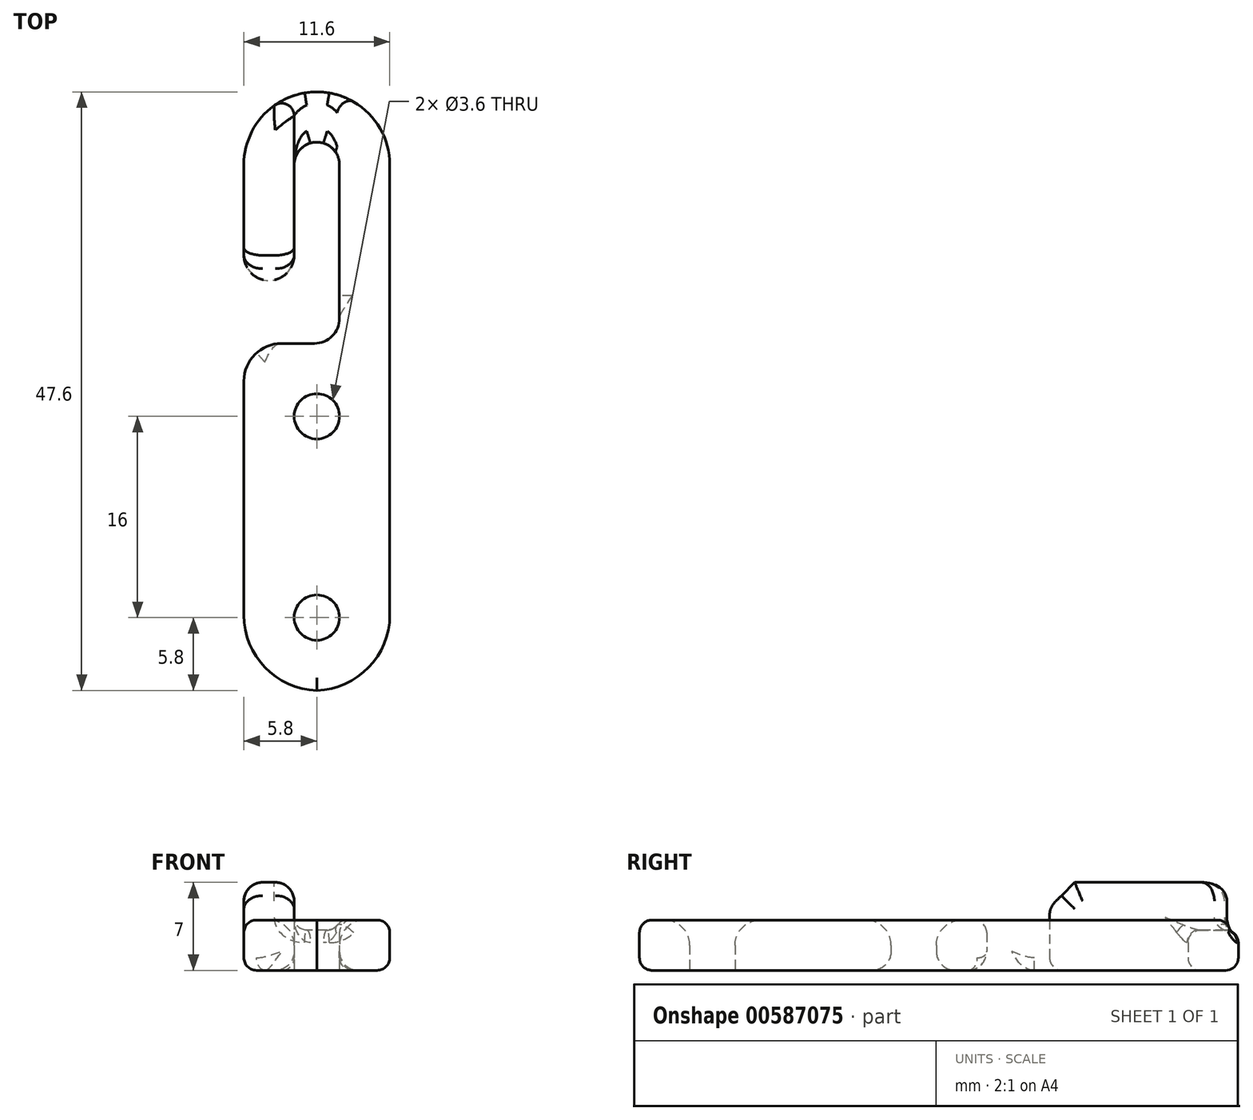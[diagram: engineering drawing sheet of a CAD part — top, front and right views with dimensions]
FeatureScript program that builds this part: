
annotation { "Feature Type Name" : "Feature", "Feature Type Description" : "" }
export const myFeature = defineFeature(function(context is Context, id is Id, definition is map)
    precondition{}
    {
        {
            var Q0;
            Q0=qCreatedBy(makeId("Top.planeOp"),FACE);
            var sketch = newSketch(context, id + "F0", { "sketchPlane" : qUnion([Q0])});
            skCircle(sketch, "E0", {"center": v(0, 0) * mm, "radius": 1.8 * mm});
            skCircle(sketch, "E1", {"center": v(0, -16) * mm, "radius": 1.8 * mm});
            skLineSegment(sketch, "E2", {"start": v(0, 0) * mm, "end": v(0, 20) * mm, "construction": true});
            skLineSegment(sketch, "E3", {"start": v(0, 0) * mm, "end": v(0, -16) * mm, "construction": true});
            skLineSegment(sketch, "E4.top", {"start": v(0.2, -21.8) * mm, "end": v(-0.2, -21.8) * mm});
            skLineSegment(sketch, "E4.left", {"start": v(5.8, 20) * mm, "end": v(5.8, 12.8) * mm});
            skLineSegment(sketch, "E4.right", {"start": v(-5.8, 2.8) * mm, "end": v(-5.8, -15.8) * mm});
            skPoint(sketch, "E5.visualSharp", {"position": v(5.8, -21.8) * mm});
            skArc(sketch, "E5.filletArc", {"start": v(-0.2, -21.8) * mm, "mid": v(4.04, -20.04) * mm, "end": v(5.8, -15.8) * mm});
            skPoint(sketch, "E6.visualSharp", {"position": v(-5.8, -21.8) * mm});
            skArc(sketch, "E6.filletArc", {"start": v(-5.8, -15.8) * mm, "mid": v(-4.04, -20.04) * mm, "end": v(0.2, -21.8) * mm});
            skLineSegment(sketch, "E7", {"start": v(0, 20) * mm, "end": v(1.8, 20) * mm, "construction": true});
            skLineSegment(sketch, "E8.trimOffspring", {"start": v(5.8, 12.8) * mm, "end": v(5.8, -15.8) * mm});
            skLineSegment(sketch, "E9", {"start": v(-1.8, 20) * mm, "end": v(-1.8, 12.8) * mm});
            skLineSegment(sketch, "E10", {"start": v(1.8, 20) * mm, "end": v(1.8, 7.8) * mm});
            skPoint(sketch, "E11.trimOffspring.start.orphan", {"position": v(-1.8, 12.8) * mm});
            skArc(sketch, "E12", {"start": v(1.8, 20) * mm, "mid": v(0, 21.8) * mm, "end": v(-1.8, 20) * mm});
            skArc(sketch, "E13", {"start": v(-5.8, 20) * mm, "mid": v(0, 25.8) * mm, "end": v(5.8, 20) * mm});
            skLineSegment(sketch, "E14", {"start": v(-5.8, 20) * mm, "end": v(-5.8, 12.8) * mm});
            skArc(sketch, "E15", {"start": v(-5.8, 12.8) * mm, "mid": v(-3.8, 10.8) * mm, "end": v(-1.8, 12.8) * mm});
            skPoint(sketch, "E16.orphan", {"position": v(-1.8, 5.8) * mm});
            skLineSegment(sketch, "E17", {"start": v(-2.8, 5.8) * mm, "end": v(-0.2, 5.8) * mm});
            skPoint(sketch, "E18.orphan", {"position": v(1.8, 12.8) * mm});
            skPoint(sketch, "E19.visualSharp", {"position": v(-5.8, 5.8) * mm});
            skArc(sketch, "E19.filletArc", {"start": v(-2.8, 5.8) * mm, "mid": v(-4.92, 4.92) * mm, "end": v(-5.8, 2.8) * mm});
            skPoint(sketch, "E20.visualSharp", {"position": v(1.8, 5.8) * mm});
            skArc(sketch, "E20.filletArc", {"start": v(-0.2, 5.8) * mm, "mid": v(1.21, 6.39) * mm, "end": v(1.8, 7.8) * mm});
            skSolve(sketch);
        }
        {
            var Q0;
            Q0=makeQuery(id+"F0.imprint","IMPRINT",FACE,{"disambiguationData":[TD([[makeQuery(id+"F0.imprint","IMPRINT",EDGE,{"derivedFrom":sQuery(id+"F0.wireOp",EDGE,"E0")}),-1.0]])]});
            extrude(context, id + "F1", {"entities" : qUnion([Q0]), "depth" : 4 * mm, "offsetDistance" : 25 * mm});
        }
        {
            var Q0;
            Q0=makeQuery(id+"F1.opExtrude","CAP_EDGE",EDGE,{"disambiguationData":[OSD([sQuery(id+"F0.wireOp",EDGE,"E0")])],"isStart":false});
            var Q1;
            Q1=makeQuery(id+"F1.opExtrude","CAP_EDGE",EDGE,{"disambiguationData":[OSD([sQuery(id+"F0.wireOp",EDGE,"E1")])],"isStart":false});
            fillet(context, id + "F2", {"entities" : qUnion([Q0, Q1]), "radius" : 2 * mm, "tangentPropagation" : true, "allowEdgeOverflow" : false});
        }
        {
            var Q0;
            Q0=makeQuery(id+"F1.opExtrude","CAP_EDGE",EDGE,{"disambiguationData":[OSD([sQuery(id+"F0.wireOp",EDGE,"E0")])],"isStart":true});
            var Q1;
            Q1=makeQuery(id+"F1.opExtrude","CAP_EDGE",EDGE,{"disambiguationData":[OSD([sQuery(id+"F0.wireOp",EDGE,"RurybiIE-2Qs8-uj2R-1JhG-sVs6zd4Z8fUQ")])],"isStart":true});
            var Q2;
            Q2=makeQuery(id+"F1.opExtrude","CAP_EDGE",EDGE,{"disambiguationData":[OSD([sQuery(id+"F0.wireOp",EDGE,"315a471d-3a10-48b4-a05f-508db2f02c06.filletArc")])],"isStart":true});
            fillet(context, id + "F3", {"entities" : qUnion([Q0, Q1, Q2]), "radius" : 1.5 * mm, "allowEdgeOverflow" : false});
        }
        {
            var Q0;
            Q0=makeQuery(id+"F1.opExtrude","CAP_EDGE",EDGE,{"disambiguationData":[OSD([sQuery(id+"F0.wireOp",EDGE,"E17")])],"isStart":true});
            var Q1;
            Q1=makeQuery(id+"F1.opExtrude","CAP_EDGE",EDGE,{"disambiguationData":[OSD([sQuery(id+"F0.wireOp",EDGE,"E20.filletArc")])],"isStart":true});
            fillet(context, id + "F4", {"entities" : qUnion([Q0, Q1]), "radius" : 1.5 * mm, "allowEdgeOverflow" : false});
        }
        {
            var Q0;
            Q0=makeQuery(id+"F1.opExtrude","CAP_FACE",FACE,{"disambiguationData":[OSD([sQuery(id+"F0.wireOp",EDGE,"E0"),sQuery(id+"F0.wireOp",EDGE,"E1"),sQuery(id+"F0.wireOp",EDGE,"E4.left"),sQuery(id+"F0.wireOp",EDGE,"E4.right"),sQuery(id+"F0.wireOp",EDGE,"E5.filletArc"),sQuery(id+"F0.wireOp",EDGE,"E6.filletArc"),sQuery(id+"F0.wireOp",EDGE,"E8.trimOffspring"),sQuery(id+"F0.wireOp",EDGE,"E9"),sQuery(id+"F0.wireOp",EDGE,"E10"),sQuery(id+"F0.wireOp",EDGE,"E12"),sQuery(id+"F0.wireOp",EDGE,"E13"),sQuery(id+"F0.wireOp",EDGE,"E14"),sQuery(id+"F0.wireOp",EDGE,"E15"),sQuery(id+"F0.wireOp",EDGE,"E17"),sQuery(id+"F0.wireOp",EDGE,"E19.filletArc"),sQuery(id+"F0.wireOp",EDGE,"E20.filletArc")])],"isStart":false});
            var sketch = newSketch(context, id + "F5", { "sketchPlane" : qUnion([Q0])});
            skArc(sketch, "E21.0.0", {"start": v(-5.8, -15.8) * mm, "mid": v(-4.11, -19.97) * mm, "end": v(0, -21.8) * mm});
            skArc(sketch, "E21.0.1", {"start": v(0, -21.8) * mm, "mid": v(4.11, -19.97) * mm, "end": v(5.8, -15.8) * mm});
            skLineSegment(sketch, "E21.0.2", {"start": v(5.8, -15.8) * mm, "end": v(5.8, 20) * mm});
            skArc(sketch, "E21.0.3", {"start": v(5.8, 20) * mm, "mid": v(0, 25.8) * mm, "end": v(-5.8, 20) * mm});
            skLineSegment(sketch, "E21.0.4", {"start": v(-5.8, 20) * mm, "end": v(-5.8, 12.8) * mm});
            skArc(sketch, "E21.0.5", {"start": v(-5.8, 12.8) * mm, "mid": v(-3.8, 10.8) * mm, "end": v(-1.8, 12.8) * mm});
            skLineSegment(sketch, "E21.0.6", {"start": v(-1.8, 12.8) * mm, "end": v(-1.8, 20) * mm});
            skArc(sketch, "E21.0.7", {"start": v(-1.8, 20) * mm, "mid": v(0, 21.8) * mm, "end": v(1.8, 20) * mm});
            skLineSegment(sketch, "E21.0.8", {"start": v(1.8, 20) * mm, "end": v(1.8, 7.8) * mm});
            skArc(sketch, "E21.0.9", {"start": v(1.8, 7.8) * mm, "mid": v(1.21, 6.39) * mm, "end": v(-0.2, 5.8) * mm});
            skLineSegment(sketch, "E21.0.10", {"start": v(-0.2, 5.8) * mm, "end": v(-2.8, 5.8) * mm});
            skArc(sketch, "E21.0.11", {"start": v(-2.8, 5.8) * mm, "mid": v(-4.92, 4.92) * mm, "end": v(-5.8, 2.8) * mm});
            skLineSegment(sketch, "E21.0.12", {"start": v(-5.8, 2.8) * mm, "end": v(-5.8, -15.8) * mm});
            skLineSegment(sketch, "E22", {"start": v(-1.8, 20) * mm, "end": v(-5.8, 20) * mm});
            skLineSegment(sketch, "E23", {"start": v(-1.8, 12.8) * mm, "end": v(-5.8, 12.8) * mm});
            skLineSegment(sketch, "E24", {"start": v(-1.8, 20) * mm, "end": v(-1.8, 30.41) * mm});
            skSolve(sketch);
        }
        {
            var Q0;
            Q0=makeQuery(id+"F5.imprint","IMPRINT",FACE,{"disambiguationData":[TD([[makeQuery(id+"F5.imprint","IMPRINT",EDGE,{"derivedFrom":sQuery(id+"F5.wireOp",EDGE,"E21.0.4")}),1.0]])]});
            var Q1;
            {var subQ0=sQuery(id+"F5.wireOp",EDGE,"E22");Q1=makeQuery(id+"F5.imprint","IMPRINT",FACE,{"disambiguationData":[TD([[makeQuery(id+"F5.imprint","IMPRINT",EDGE,{"derivedFrom":subQ0}),-1.0]])]});}
            var Q2;
            Q2=makeQuery(id+"F5.imprint","IMPRINT",FACE,{"disambiguationData":[TD([[makeQuery(id+"F5.imprint","IMPRINT",EDGE,{"derivedFrom":sQuery(id+"F5.wireOp",EDGE,"E21.0.5")}),1.0]])]});
            extrude(context, id + "F6", {"entities" : qUnion([Q0, Q1, Q2]), "operationType" : NewBodyOperationType.ADD, "depth" : 3 * mm, "offsetDistance" : 25 * mm});
        }
        {
            var Q0;
            Q0=makeQuery(id+"F6.boolean.opBoolean","MERGE",FACE,{"derivedFrom":[makeQuery(id+"F1.opExtrude","SWEPT_FACE",FACE,{"disambiguationData":[OSD([sQuery(id+"F0.wireOp",EDGE,"E14")])]}),makeQuery(id+"F6.opExtrude","SWEPT_FACE",FACE,{"disambiguationData":[OSD([sQuery(id+"F5.wireOp",EDGE,"E21.0.4")])]})]});
            var sketch = newSketch(context, id + "F7", { "sketchPlane" : qUnion([Q0])});
            skPoint(sketch, "E25.1", {"position": v(-12.8, 7) * mm});
            skLineSegment(sketch, "E25.2", {"start": v(-20, 7) * mm, "end": v(-12.8, 7) * mm});
            skLineSegment(sketch, "E25.3", {"start": v(-12.8, 7) * mm, "end": v(-12.8, 1) * mm});
            skLineSegment(sketch, "E26", {"start": v(-12.8, 7) * mm, "end": v(-10.23, 4.43) * mm});
            skLineSegment(sketch, "E27", {"start": v(-10.23, 4.43) * mm, "end": v(-10.23, 7) * mm});
            skLineSegment(sketch, "E28", {"start": v(-10.23, 7) * mm, "end": v(-12.8, 7) * mm});
            skSolve(sketch);
        }
        {
            var Q0;
            Q0 = qSketchRegion(id + "F7", true);
            extrude(context, id + "F8", {"entities" : qUnion([Q0]), "operationType" : NewBodyOperationType.REMOVE, "endBound" : BoundingType.THROUGH_ALL, "oppositeDirection" : true, "depth" : 25 * mm, "offsetDistance" : 25 * mm});
        }
        {
            var Q0;
            Q0=makeQuery(id+"F8.boolean.opBoolean","INTERSECT",EDGE,{"derivedFrom":[makeQuery(id+"F6.boolean.opBoolean","MERGE",FACE,{"derivedFrom":[makeQuery(id+"F1.opExtrude","SWEPT_FACE",FACE,{"disambiguationData":[OSD([sQuery(id+"F0.wireOp",EDGE,"E15")])]}),makeQuery(id+"F6.opExtrude","SWEPT_FACE",FACE,{"disambiguationData":[OSD([sQuery(id+"F5.wireOp",EDGE,"E21.0.5")])]})]}),makeQuery(id+"F8.opExtrude","SWEPT_FACE",FACE,{"disambiguationData":[OSD([sQuery(id+"F7.wireOp",EDGE,"E26")])]})]});
            var Q1;
            Q1=makeQuery(id+"F6.opExtrude","CAP_EDGE",EDGE,{"disambiguationData":[OSD([sQuery(id+"F5.wireOp",EDGE,"E21.0.4")])],"isStart":false});
            var Q2;
            Q2=makeQuery(id+"F6.opExtrude","CAP_EDGE",EDGE,{"disambiguationData":[OSD([sQuery(id+"F5.wireOp",EDGE,"E21.0.3")])],"isStart":false});
            var Q3;
            Q3=makeQuery(id+"F6.opExtrude","CAP_EDGE",EDGE,{"disambiguationData":[OSD([sQuery(id+"F5.wireOp",EDGE,"E21.0.6"),sQuery(id+"F5.wireOp",EDGE,"E24")])],"isStart":false});
            fillet(context, id + "F9", {"entities" : qUnion([Q0, Q1, Q2, Q3]), "radius" : 1.5 * mm, "tangentPropagation" : true, "allowEdgeOverflow" : false});
        }
        {
            var Q0;
            Q0=makeQuery(id+"F1.opExtrude","CAP_FACE",FACE,{"disambiguationData":[OSD([sQuery(id+"F0.wireOp",EDGE,"E0"),sQuery(id+"F0.wireOp",EDGE,"E1"),sQuery(id+"F0.wireOp",EDGE,"E4.left"),sQuery(id+"F0.wireOp",EDGE,"E4.right"),sQuery(id+"F0.wireOp",EDGE,"E5.filletArc"),sQuery(id+"F0.wireOp",EDGE,"E6.filletArc"),sQuery(id+"F0.wireOp",EDGE,"E8.trimOffspring"),sQuery(id+"F0.wireOp",EDGE,"E9"),sQuery(id+"F0.wireOp",EDGE,"E10"),sQuery(id+"F0.wireOp",EDGE,"E12"),sQuery(id+"F0.wireOp",EDGE,"E13"),sQuery(id+"F0.wireOp",EDGE,"E14"),sQuery(id+"F0.wireOp",EDGE,"E15"),sQuery(id+"F0.wireOp",EDGE,"E17"),sQuery(id+"F0.wireOp",EDGE,"E19.filletArc"),sQuery(id+"F0.wireOp",EDGE,"E20.filletArc")])],"isStart":false});
            var sketch = newSketch(context, id + "F10", { "sketchPlane" : qUnion([Q0])});
            skArc(sketch, "E29.0.0", {"start": v(5.8, 20) * mm, "mid": v(3.4, 24.7) * mm, "end": v(-1.8, 25.51) * mm});
            skLineSegment(sketch, "E29.0.1", {"start": v(-1.8, 25.51) * mm, "end": v(-1.8, 20) * mm});
            skArc(sketch, "E29.0.2", {"start": v(-1.8, 20) * mm, "mid": v(0, 21.8) * mm, "end": v(1.8, 20) * mm});
            skLineSegment(sketch, "E29.0.3", {"start": v(1.8, 20) * mm, "end": v(1.8, 7.8) * mm});
            skArc(sketch, "E29.0.4", {"start": v(1.8, 7.8) * mm, "mid": v(1.21, 6.39) * mm, "end": v(-0.2, 5.8) * mm});
            skLineSegment(sketch, "E29.0.5", {"start": v(-0.2, 5.8) * mm, "end": v(-2.8, 5.8) * mm});
            skArc(sketch, "E29.0.6", {"start": v(-2.8, 5.8) * mm, "mid": v(-4.92, 4.92) * mm, "end": v(-5.8, 2.8) * mm});
            skLineSegment(sketch, "E29.0.7", {"start": v(-5.8, 2.8) * mm, "end": v(-5.8, -15.8) * mm});
            skArc(sketch, "E29.0.8", {"start": v(-5.8, -15.8) * mm, "mid": v(-4.11, -19.97) * mm, "end": v(0, -21.8) * mm});
            skArc(sketch, "E29.0.9", {"start": v(0, -21.8) * mm, "mid": v(4.11, -19.97) * mm, "end": v(5.8, -15.8) * mm});
            skLineSegment(sketch, "E29.0.10", {"start": v(5.8, -15.8) * mm, "end": v(5.8, 20) * mm});
            skLineSegment(sketch, "E30", {"start": v(1.8, 20) * mm, "end": v(1.8, 30.8) * mm});
            skSolve(sketch);
        }
        {
            var Q0;
            {var subQ0=sQuery(id+"F10.wireOp",EDGE,"E29.0.1");Q0=makeQuery(id+"F10.imprint","IMPRINT",FACE,{"disambiguationData":[TD([[makeQuery(id+"F10.imprint","IMPRINT",EDGE,{"derivedFrom":subQ0}),1.0]])]});}
            extrude(context, id + "F11", {"entities" : qUnion([Q0]), "operationType" : NewBodyOperationType.REMOVE, "oppositeDirection" : true, "depth" : 0.8 * mm, "offsetDistance" : 25 * mm});
        }
        {
            var Q0;
            Q0=makeQuery(id+"F11.boolean.opBoolean","COPY",EDGE,{"derivedFrom":makeQuery(id+"F11.opExtrude","CAP_EDGE",EDGE,{"disambiguationData":[OSD([sQuery(id+"F10.wireOp",EDGE,"E29.0.1")])],"isStart":false})});
            var Q1;
            Q1=makeQuery(id+"F11.boolean.opBoolean","COPY",EDGE,{"derivedFrom":makeQuery(id+"F11.opExtrude","CAP_EDGE",EDGE,{"disambiguationData":[OSD([sQuery(id+"F10.wireOp",EDGE,"E30")])],"isStart":false})});
            fillet(context, id + "F12", {"entities" : qUnion([Q0, Q1]), "radius" : 1 * mm, "tangentPropagation" : true, "allowEdgeOverflow" : false});
        }
        {
            var Q0;
            Q0=makeQuery(id+"F12.opFillet","BLEND_EDGE",EDGE,{"blendedFrom":[makeQuery(id+"F11.boolean.opBoolean","COPY",EDGE,{"derivedFrom":makeQuery(id+"F11.opExtrude","CAP_EDGE",EDGE,{"disambiguationData":[OSD([sQuery(id+"F10.wireOp",EDGE,"E29.0.1")])],"isStart":false})}),makeQuery(id+"F1.opExtrude","SWEPT_FACE",FACE,{"disambiguationData":[OSD([sQuery(id+"F0.wireOp",EDGE,"E12")])]})],"blendedInto":[makeQuery(id+"F1.opExtrude","SWEPT_FACE",FACE,{"disambiguationData":[OSD([sQuery(id+"F0.wireOp",EDGE,"E12")])]})]});
            var Q1;
            Q1=makeQuery(id+"F11.boolean.opBoolean","COPY",EDGE,{"derivedFrom":makeQuery(id+"F11.opExtrude","CAP_EDGE",EDGE,{"disambiguationData":[OSD([sQuery(id+"F10.wireOp",EDGE,"E29.0.2")])],"isStart":false})});
            var Q2;
            Q2=makeQuery(id+"F12.opFillet","BLEND_EDGE",EDGE,{"blendedFrom":[makeQuery(id+"F11.boolean.opBoolean","COPY",EDGE,{"derivedFrom":makeQuery(id+"F11.opExtrude","CAP_EDGE",EDGE,{"disambiguationData":[OSD([sQuery(id+"F10.wireOp",EDGE,"E30")])],"isStart":false})}),makeQuery(id+"F1.opExtrude","SWEPT_FACE",FACE,{"disambiguationData":[OSD([sQuery(id+"F0.wireOp",EDGE,"E12")])]})],"blendedInto":[makeQuery(id+"F1.opExtrude","SWEPT_FACE",FACE,{"disambiguationData":[OSD([sQuery(id+"F0.wireOp",EDGE,"E12")])]})]});
            fillet(context, id + "F13", {"entities" : qUnion([Q0, Q1, Q2]), "radius" : 1 * mm, "allowEdgeOverflow" : false});
        }
        {
            var Q0;
            Q0=makeQuery(id+"F11.boolean.opBoolean","MERGE",EDGE,{"derivedFrom":[makeQuery(id+"F6.opExtrude","SWEPT_EDGE",EDGE,{"disambiguationData":[OSD([sQuery(id+"F5.wireOp",EDGE,"E21.0.3"),sQuery(id+"F5.wireOp",EDGE,"E24")])]}),makeQuery(id+"F11.opExtrude","SWEPT_EDGE",EDGE,{"disambiguationData":[OSD([sQuery(id+"F10.wireOp",EDGE,"E29.0.0"),sQuery(id+"F10.wireOp",EDGE,"E29.0.1")])]})]});
            var Q1;
            Q1=makeQuery(id+"F9.opFillet","BLEND_EDGE",EDGE,{"blendedFrom":[makeQuery(id+"F6.opExtrude","CAP_EDGE",EDGE,{"disambiguationData":[OSD([sQuery(id+"F5.wireOp",EDGE,"E21.0.3")])],"isStart":false}),makeQuery(id+"F6.opExtrude","CAP_EDGE",EDGE,{"disambiguationData":[OSD([sQuery(id+"F5.wireOp",EDGE,"E21.0.6"),sQuery(id+"F5.wireOp",EDGE,"E24")])],"isStart":false})],"blendedInto":[]});
            fillet(context, id + "F14", {"entities" : qUnion([Q0, Q1]), "radius" : 1 * mm, "tangentPropagation" : true, "allowEdgeOverflow" : false});
        }
        {
            var Q0;
            Q0=makeQuery(id+"F1.opExtrude","CAP_EDGE",EDGE,{"disambiguationData":[OSD([sQuery(id+"F0.wireOp",EDGE,"E4.right")])],"isStart":false});
            var Q1;
            Q1=makeQuery(id+"F1.opExtrude","CAP_EDGE",EDGE,{"disambiguationData":[OSD([sQuery(id+"F0.wireOp",EDGE,"E19.filletArc")])],"isStart":false});
            var Q2;
            Q2=makeQuery(id+"F1.opExtrude","CAP_EDGE",EDGE,{"disambiguationData":[OSD([sQuery(id+"F0.wireOp",EDGE,"E17")])],"isStart":false});
            var Q3;
            Q3=makeQuery(id+"F1.opExtrude","CAP_EDGE",EDGE,{"disambiguationData":[OSD([sQuery(id+"F0.wireOp",EDGE,"E20.filletArc")])],"isStart":false});
            var Q4;
            Q4=makeQuery(id+"F1.opExtrude","CAP_EDGE",EDGE,{"disambiguationData":[OSD([sQuery(id+"F0.wireOp",EDGE,"E5.filletArc")])],"isStart":false});
            var Q5;
            Q5=makeQuery(id+"F1.opExtrude","CAP_EDGE",EDGE,{"disambiguationData":[OSD([sQuery(id+"F0.wireOp",EDGE,"E4.left"),sQuery(id+"F0.wireOp",EDGE,"E8.trimOffspring")])],"isStart":false});
            var Q6;
            Q6=makeQuery(id+"F1.opExtrude","CAP_EDGE",EDGE,{"disambiguationData":[OSD([sQuery(id+"F0.wireOp",EDGE,"E5.filletArc")])],"isStart":true});
            var Q7;
            Q7=makeQuery(id+"F1.opExtrude","CAP_EDGE",EDGE,{"disambiguationData":[OSD([sQuery(id+"F0.wireOp",EDGE,"E4.left"),sQuery(id+"F0.wireOp",EDGE,"E8.trimOffspring")])],"isStart":true});
            var Q8;
            Q8=makeQuery(id+"F1.opExtrude","CAP_EDGE",EDGE,{"disambiguationData":[OSD([sQuery(id+"F0.wireOp",EDGE,"E13")])],"isStart":true});
            var Q9;
            Q9=makeQuery(id+"F1.opExtrude","CAP_EDGE",EDGE,{"disambiguationData":[OSD([sQuery(id+"F0.wireOp",EDGE,"E14")])],"isStart":true});
            var Q10;
            Q10=makeQuery(id+"F1.opExtrude","CAP_EDGE",EDGE,{"disambiguationData":[OSD([sQuery(id+"F0.wireOp",EDGE,"E15")])],"isStart":true});
            var Q11;
            Q11=makeQuery(id+"F1.opExtrude","CAP_EDGE",EDGE,{"disambiguationData":[OSD([sQuery(id+"F0.wireOp",EDGE,"E9")])],"isStart":true});
            var Q12;
            Q12=makeQuery(id+"F1.opExtrude","CAP_EDGE",EDGE,{"disambiguationData":[OSD([sQuery(id+"F0.wireOp",EDGE,"E12")])],"isStart":true});
            var Q13;
            Q13=makeQuery(id+"F1.opExtrude","CAP_EDGE",EDGE,{"disambiguationData":[OSD([sQuery(id+"F0.wireOp",EDGE,"E10")])],"isStart":true});
            var Q14;
            Q14=makeQuery(id+"F1.opExtrude","CAP_EDGE",EDGE,{"disambiguationData":[OSD([sQuery(id+"F0.wireOp",EDGE,"E6.filletArc")])],"isStart":true});
            var Q15;
            Q15=makeQuery(id+"F1.opExtrude","CAP_EDGE",EDGE,{"disambiguationData":[OSD([sQuery(id+"F0.wireOp",EDGE,"E4.right")])],"isStart":true});
            fillet(context, id + "F15", {"entities" : qUnion([Q0, Q1, Q2, Q3, Q4, Q5, Q6, Q7, Q8, Q9, Q10, Q11, Q12, Q13, Q14, Q15]), "radius" : 1 * mm, "tangentPropagation" : true, "allowEdgeOverflow" : false});
        }
    });
